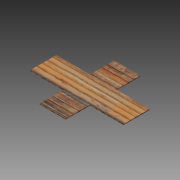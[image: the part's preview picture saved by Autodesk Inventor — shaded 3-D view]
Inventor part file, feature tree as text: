
AUTODESK INVENTOR PART (.ipt)
format: ipt  version: 2015 SP1 (Build 190203100, 203)  size: 101,376 bytes
history: native  units: in
note: dims shown in document units (in); Inventor stores cm internally (conversion verified against a paired STEP export)
features: extrude x1, sketch x1
ambient origin geometry x8: Origin, YZ Plane, XZ Plane, XY Plane, X Axis, Y Axis, Z Axis, Center Point
bodies: Solid1 (feature_tree)
feature tree (2):
  extrude  "Extrusion1"  Depth=0.25in TaperAngle=0.0deg
  sketch  "Sketch1"  dims[d1=7.0in d2=0.25in d3=0.0in d5=7.0in d6=25.0in d7=20.0in]
